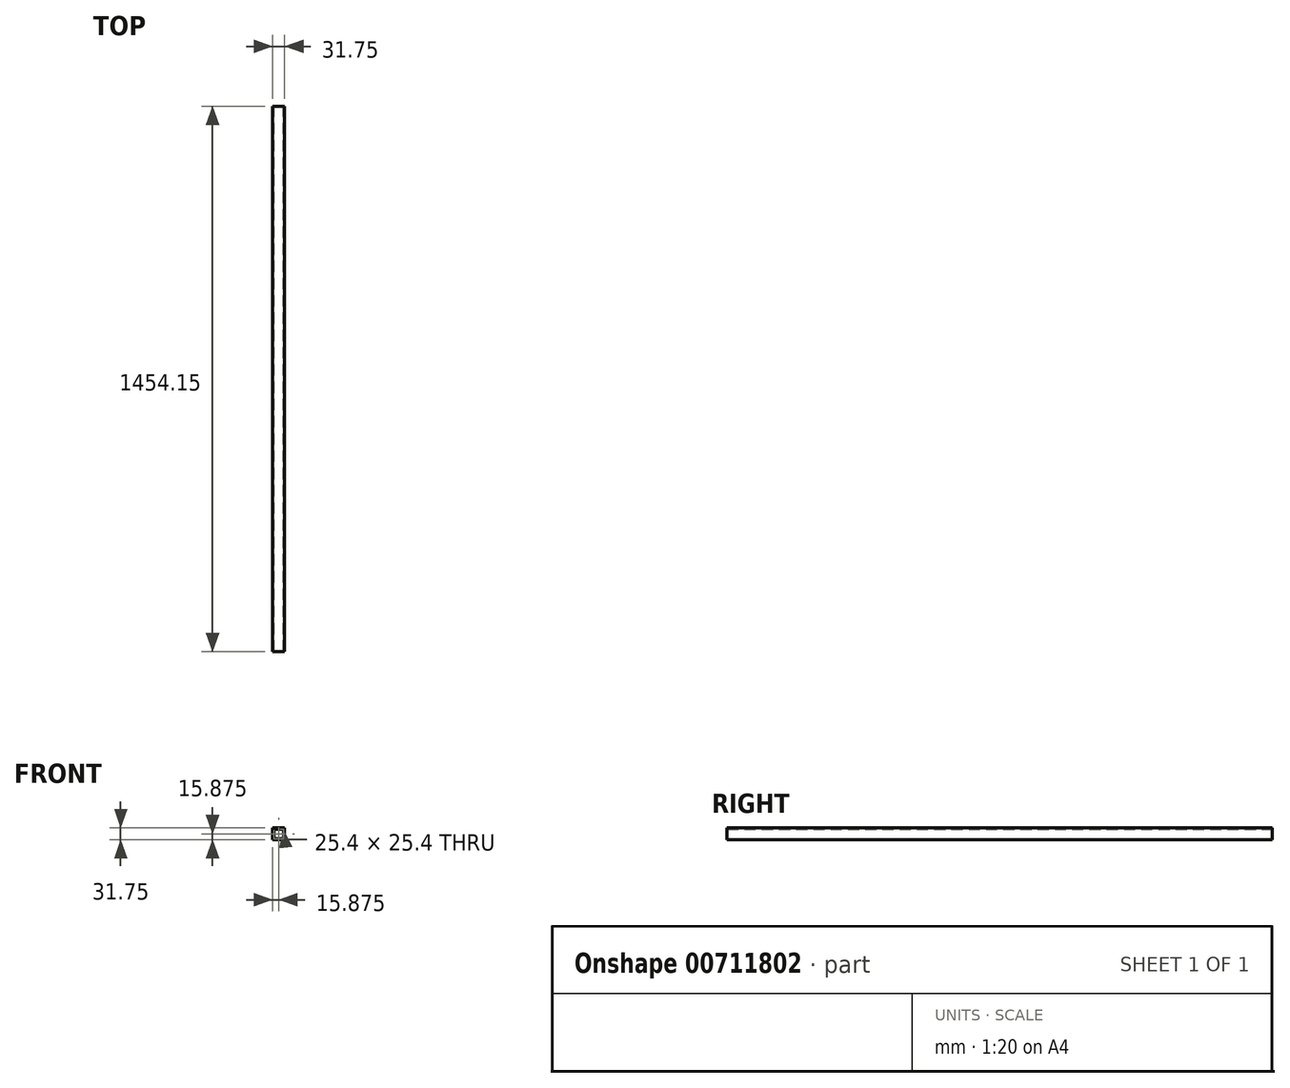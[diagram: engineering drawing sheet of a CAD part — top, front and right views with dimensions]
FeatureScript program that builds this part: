
annotation { "Feature Type Name" : "Feature", "Feature Type Description" : "" }
export const myFeature = defineFeature(function(context is Context, id is Id, definition is map)
    precondition{}
    {
        {
            var Q0;
            Q0=qCreatedBy(makeId("Front.planeOp"),FACE);
            var sketch = newSketch(context, id + "F0", { "sketchPlane" : qUnion([Q0])});
            skLineSegment(sketch, "E0.bottom", {"start": v(0, 0) * mm, "end": v(31.75, 0) * mm});
            skLineSegment(sketch, "E0.top", {"start": v(0, 31.75) * mm, "end": v(31.75, 31.75) * mm});
            skLineSegment(sketch, "E0.left", {"start": v(0, 0) * mm, "end": v(0, 31.75) * mm});
            skLineSegment(sketch, "E0.right", {"start": v(31.75, 0) * mm, "end": v(31.75, 31.75) * mm});
            skLineSegment(sketch, "E1.bottom", {"start": v(3.18, 3.18) * mm, "end": v(28.58, 3.18) * mm});
            skLineSegment(sketch, "E1.top", {"start": v(3.17, 28.58) * mm, "end": v(28.58, 28.58) * mm});
            skLineSegment(sketch, "E1.left", {"start": v(3.17, 3.18) * mm, "end": v(3.17, 28.58) * mm});
            skLineSegment(sketch, "E1.right", {"start": v(28.58, 3.18) * mm, "end": v(28.58, 28.58) * mm});
            skSolve(sketch);
        }
        {
            var Q0;
            Q0 = qSketchRegion(id + "F0", true);
            extrude(context, id + "F1", {"entities" : qUnion([Q0]), "depth" : 1454.15 * mm, "offsetDistance" : 25.4 * mm});
        }
    });
